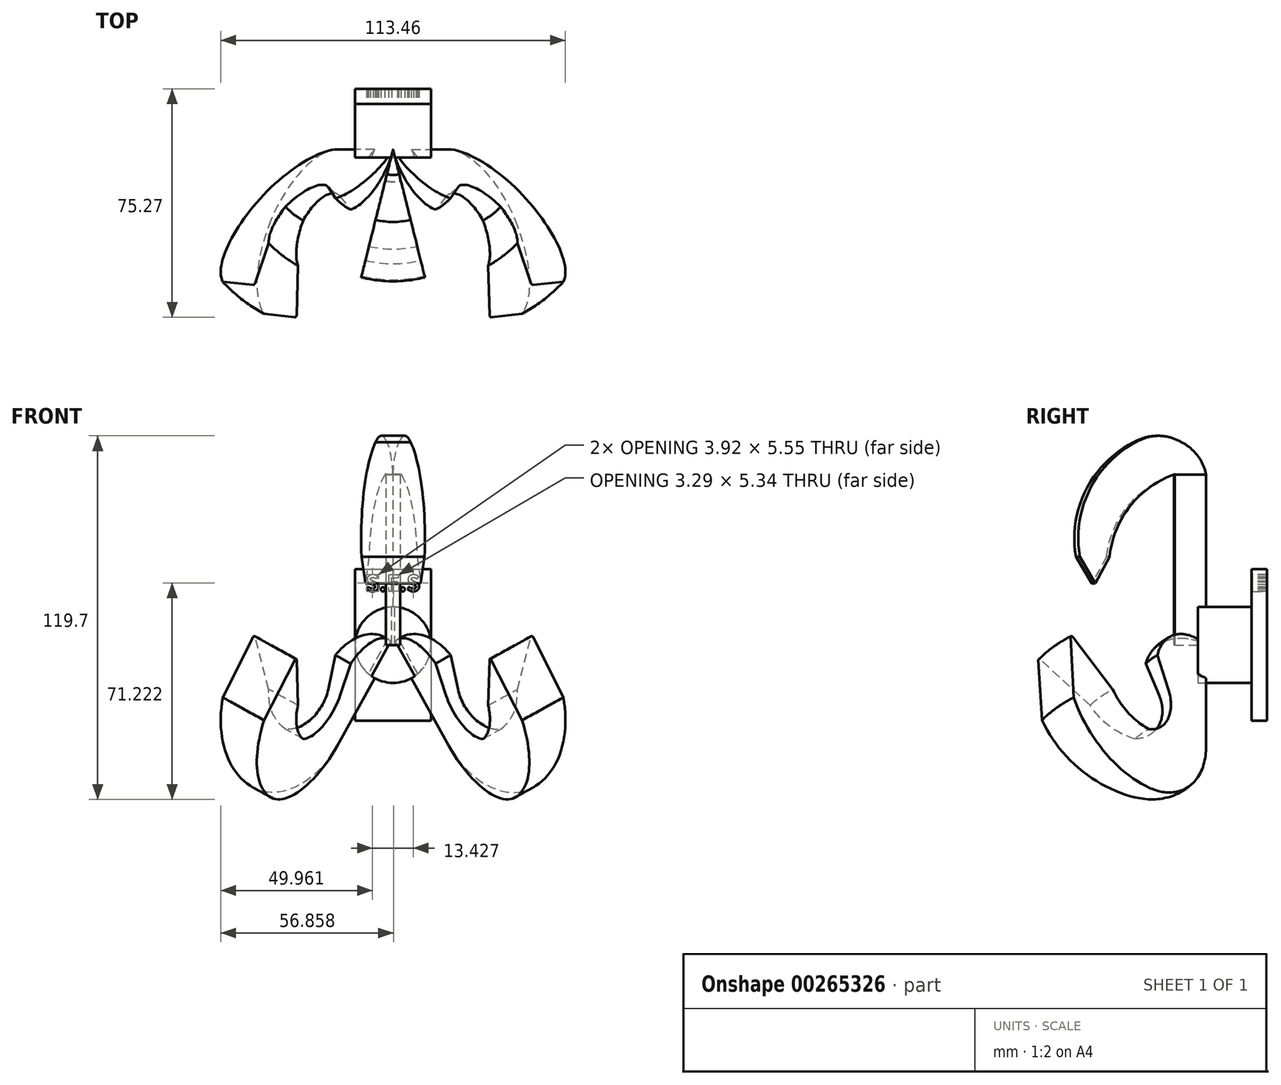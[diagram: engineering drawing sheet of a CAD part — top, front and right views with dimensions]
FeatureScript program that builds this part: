
annotation { "Feature Type Name" : "Feature", "Feature Type Description" : "" }
export const myFeature = defineFeature(function(context is Context, id is Id, definition is map)
    precondition{}
    {
        {
            var Q0;
            Q0=qCreatedBy(makeId("Front.planeOp"),FACE);
            var sketch = newSketch(context, id + "F0", { "sketchPlane" : qUnion([Q0])});
            skLineSegment(sketch, "E0", {"start": v(0, 0) * mm, "end": v(18.35, -33.17) * mm});
            skArc(sketch, "E1", {"start": v(18.35, -33.17) * mm, "mid": v(33.68, -45.34) * mm, "end": v(53.11, -43.05) * mm});
            skArc(sketch, "E2", {"start": v(53.11, -43.05) * mm, "mid": v(67.8, -28.34) * mm, "end": v(72.64, -8.13) * mm});
            skPoint(sketch, "E3.start.orphan", {"position": v(22.53, 0) * mm});
            skArc(sketch, "E4", {"start": v(42.6, -23.75) * mm, "mid": v(49.37, -17.07) * mm, "end": v(52.64, -8.13) * mm});
            skArc(sketch, "E5", {"start": v(26.08, -11.95) * mm, "mid": v(31.61, -21.66) * mm, "end": v(42.6, -23.75) * mm});
            skLineSegment(sketch, "E6", {"start": v(26.08, -11.95) * mm, "end": v(25.04, 0) * mm});
            skLineSegment(sketch, "E7", {"start": v(72.64, -8.13) * mm, "end": v(62.62, 12.93) * mm});
            skLineSegment(sketch, "E8", {"start": v(52.64, -8.13) * mm, "end": v(62.62, 12.93) * mm});
            skArc(sketch, "E9", {"start": v(25.04, 0) * mm, "mid": v(12.52, 5.52) * mm, "end": v(0, 0) * mm});
            skSolve(sketch);
        }
        {
            var Q0;
            Q0=makeQuery(id+"F0.imprint","IMPRINT",FACE,{"disambiguationData":[TD([[makeQuery(id+"F0.imprint","IMPRINT",EDGE,{"derivedFrom":sQuery(id+"F0.wireOp",EDGE,"SQxlmqEL-E3AV-UpUH-LolP-xFTiHtGifUth")}),-1.0]])]});
            var Q1;
            Q1=makeQuery(id+"F0.imprint","IMPRINT",FACE,{"disambiguationData":[TD([[makeQuery(id+"F0.imprint","IMPRINT",EDGE,{"derivedFrom":sQuery(id+"F0.wireOp",EDGE,"E0")}),1.0]])]});
            var Q2;
            Q2=sQuery(id+"F0.wireOp",EDGE,"E0");
            revolve(context, id + "F1", {"entities" : qUnion([Q0, Q1]), "axis" : qUnion([Q2]), "revolveType" : RevolveType.TWO_DIRECTIONS, "angle" : 65 * degree, "angleBack" : 47 * degree});
        }
        {
            var Q0;
            Q0=makeQuery(id+"F1.opRevolve","SWEPT_EDGE",EDGE,{"disambiguationData":[OSD([sQuery(id+"F0.wireOp",EDGE,"E7"),sQuery(id+"F0.wireOp",EDGE,"E8")])]});
            fillet(context, id + "F2", {"entities" : qUnion([Q0]), "radius" : 0.5 * mm, "tangentPropagation" : true, "allowEdgeOverflow" : false});
        }
        {
            var Q0;
            Q0=qCreatedBy(makeId("Front.planeOp"),FACE);
            var sketch = newSketch(context, id + "F3", { "sketchPlane" : qUnion([Q0])});
            skLineSegment(sketch, "E10", {"start": v(10.63, 33.68) * mm, "end": v(10.63, 0) * mm});
            skLineSegment(sketch, "E11", {"start": v(10.63, 0) * mm, "end": v(0, 0) * mm});
            skLineSegment(sketch, "E12", {"start": v(0, 0) * mm, "end": v(0, 56.08) * mm});
            skLineSegment(sketch, "E13", {"start": v(0, 56.08) * mm, "end": v(10.63, 56.08) * mm});
            skLineSegment(sketch, "E14", {"start": v(10.63, 56.08) * mm, "end": v(10.63, 0) * mm});
            skSolve(sketch);
        }
        {
            var Q0;
            Q0=qCreatedBy(makeId("Right.planeOp"),FACE);
            var sketch = newSketch(context, id + "F4", { "sketchPlane" : qUnion([Q0])});
            skLineSegment(sketch, "E15", {"start": v(-10.63, 56.07) * mm, "end": v(0, 56.07) * mm});
            skLineSegment(sketch, "E16", {"start": v(0, 65) * mm, "end": v(0, 68.75) * mm});
            skLineSegment(sketch, "E17", {"start": v(0, 65) * mm, "end": v(0, 56.07) * mm});
            skLineSegment(sketch, "E18", {"start": v(-32.8, 29.06) * mm, "end": v(-37.61, 20.26) * mm});
            skLineSegment(sketch, "E19", {"start": v(-37.61, 20.26) * mm, "end": v(-42.89, 29.06) * mm});
            skArc(sketch, "E20", {"start": v(-10.6, 56.19) * mm, "mid": v(-25.66, 45.87) * mm, "end": v(-32.8, 29.06) * mm});
            skArc(sketch, "E21", {"start": v(-23.85, 66.74) * mm, "mid": v(-39.58, 51.04) * mm, "end": v(-42.89, 29.06) * mm});
            skArc(sketch, "E22", {"start": v(-8.38, 66.74) * mm, "mid": v(-16.11, 68.85) * mm, "end": v(-23.85, 66.74) * mm});
            skArc(sketch, "E23", {"start": v(0, 56.07) * mm, "mid": v(-2.94, 62.38) * mm, "end": v(-8.38, 66.74) * mm});
            skLineSegment(sketch, "E24", {"start": v(0, 56.07) * mm, "end": v(-10.6, 56.19) * mm});
            skSolve(sketch);
        }
        {
            var Q0;
            Q0=makeQuery(id+"F4.imprint","IMPRINT",FACE,{"disambiguationData":[TD([[makeQuery(id+"F4.imprint","IMPRINT",EDGE,{"derivedFrom":sQuery(id+"F4.wireOp",EDGE,"E18")}),-1.0]])]});
            var Q1;
            Q1=sQuery(id+"F4.wireOp",EDGE,"E16");
            revolve(context, id + "F5", {"entities" : qUnion([Q0]), "axis" : qUnion([Q1]), "revolveType" : RevolveType.ONE_DIRECTION, "angle" : 14 * degree});
        }
        {
            var Q0;
            {var subQ0=sQuery(id+"F3.wireOp",EDGE,"E11");Q0=makeQuery(id+"F3.imprint","IMPRINT",FACE,{"disambiguationData":[TD([[makeQuery(id+"F3.imprint","IMPRINT",EDGE,{"derivedFrom":subQ0}),-1.0]])]});}
            var Q1;
            Q1=sQuery(id+"F3.wireOp",EDGE,"E12");
            revolve(context, id + "F6", {"operationType" : NewBodyOperationType.ADD, "entities" : qUnion([Q0]), "axis" : qUnion([Q1]), "revolveType" : RevolveType.TWO_DIRECTIONS, "oppositeDirection" : true, "angle" : 90 * degree, "angleBack" : 77.5 * degree});
        }
        {
            var Q0;
            Q0=makeQuery(id+"F5.opRevolve","SWEPT_BODY",BODY,{"disambiguationData":[OSD([sQuery(id+"F4.wireOp",EDGE,"E18"),sQuery(id+"F4.wireOp",EDGE,"E19"),sQuery(id+"F4.wireOp",EDGE,"E20"),sQuery(id+"F4.wireOp",EDGE,"E21"),sQuery(id+"F4.wireOp",EDGE,"E22"),sQuery(id+"F4.wireOp",EDGE,"E23"),sQuery(id+"F4.wireOp",EDGE,"E24")])]});
            var Q1;
            Q1=qCreatedBy(makeId("Right.planeOp"),FACE);
            mirror(context, id + "F7", {"operationType" : NewBodyOperationType.ADD, "entities" : qUnion([Q0]), "mirrorPlane" : qUnion([Q1])});
        }
        {
            var Q0;
            Q0=makeQuery(id+"F1.opRevolve","SWEPT_BODY",BODY,{"disambiguationData":[OSD([sQuery(id+"F0.wireOp",EDGE,"E0"),sQuery(id+"F0.wireOp",EDGE,"E1"),sQuery(id+"F0.wireOp",EDGE,"E2"),sQuery(id+"F0.wireOp",EDGE,"E4"),sQuery(id+"F0.wireOp",EDGE,"E5"),sQuery(id+"F0.wireOp",EDGE,"E6"),sQuery(id+"F0.wireOp",EDGE,"SQxlmqEL-E3AV-UpUH-LolP-xFTiHtGifUth"),sQuery(id+"F0.wireOp",EDGE,"E7"),sQuery(id+"F0.wireOp",EDGE,"E8")])]});
            var Q1;
            Q1=qCreatedBy(makeId("Right.planeOp"),FACE);
            mirror(context, id + "F8", {"entities" : qUnion([Q0]), "mirrorPlane" : qUnion([Q1])});
        }
        {
            var Q0;
            Q0=qCreatedBy(makeId("Front.planeOp"),FACE);
            var sketch = newSketch(context, id + "F9", { "sketchPlane" : qUnion([Q0])});
            skCircle(sketch, "E25", {"center": v(0, 0) * mm, "radius": 12.5 * mm});
            skSolve(sketch);
        }
        {
            var Q0;
            Q0 = qSketchRegion(id + "F9", true);
            extrude(context, id + "F10", {"entities" : qUnion([Q0]), "depth" : 2.7 * mm});
        }
        {
            var Q0;
            Q0 = qSketchRegion(id + "F9", true);
            extrude(context, id + "F11", {"entities" : qUnion([Q0]), "operationType" : NewBodyOperationType.ADD, "oppositeDirection" : true, "depth" : 15 * mm});
        }
        {
            var Q0;
            Q0=qCreatedBy(makeId("Front.planeOp"),FACE);
            var sketch = newSketch(context, id + "F12", { "sketchPlane" : qUnion([Q0])});
            skLineSegment(sketch, "E26.bottom", {"start": v(-12.5, 25) * mm, "end": v(12.5, 25) * mm});
            skLineSegment(sketch, "E26.top", {"start": v(-12.5, -25) * mm, "end": v(12.5, -25) * mm});
            skLineSegment(sketch, "E26.left", {"start": v(-12.5, 25) * mm, "end": v(-12.5, -25) * mm});
            skLineSegment(sketch, "E26.right", {"start": v(12.5, 25) * mm, "end": v(12.5, -25) * mm});
            skPoint(sketch, "E26.middle", {"position": v(0, 0) * mm});
            skText(sketch, "E27", { "text": "S.F.S", "fontName": "NotoSansCJKjp-Bold.otf"});
            const initialGuessF12  = {"E27": [-0.00903, 0.0177, 1, 0, 0.0052]};
            skSetInitialGuess(sketch, initialGuessF12);
            skSolve(sketch);
        }
        {
            var Q0;
            Q0=makeQuery(id+"F12.imprint","IMPRINT",FACE,{"disambiguationData":[TD([[makeQuery(id+"F12.imprint","IMPRINT",EDGE,{"derivedFrom":sQuery(id+"F12.wireOp",EDGE,"E26.bottom")}),-1.0]])]});
            extrude(context, id + "F13", {"entities" : qUnion([Q0]), "operationType" : NewBodyOperationType.ADD, "oppositeDirection" : true, "depth" : 20 * mm, "hasSecondDirection" : true, "secondDirectionOppositeDirection" : true, "secondDirectionDepth" : 15 * mm});
        }
    });
